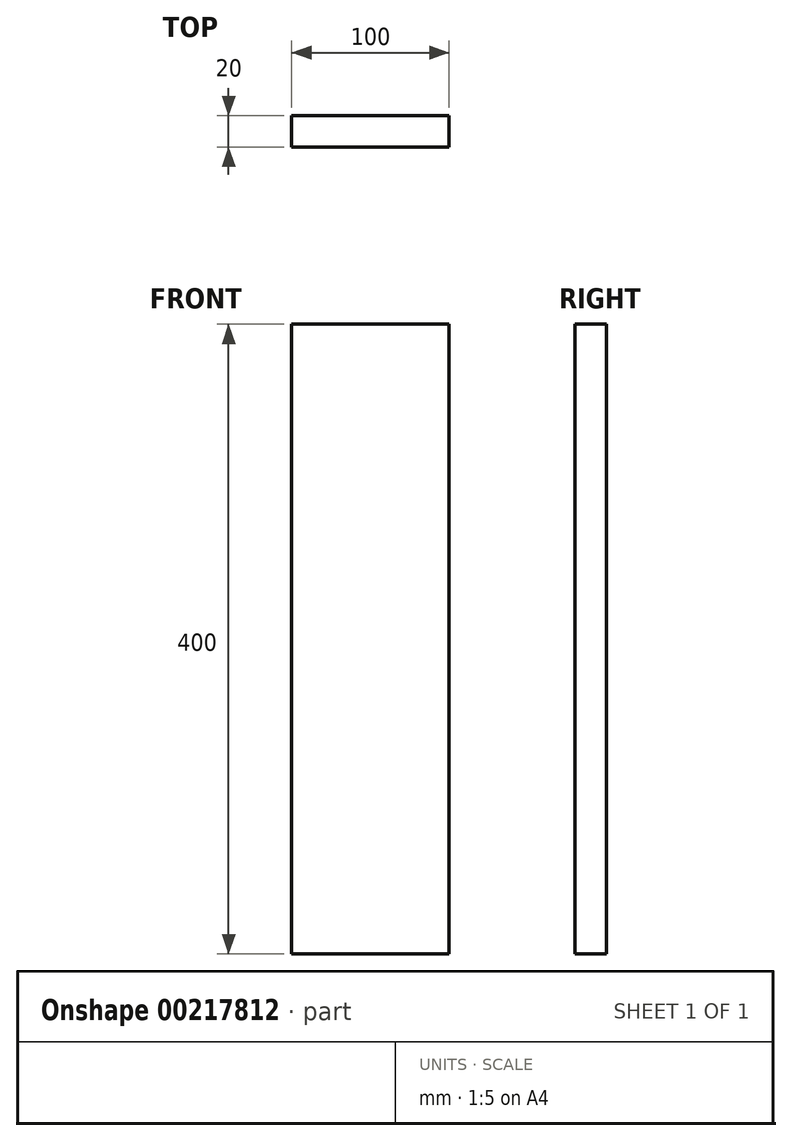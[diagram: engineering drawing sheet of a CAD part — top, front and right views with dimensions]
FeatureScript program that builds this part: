
annotation { "Feature Type Name" : "Feature", "Feature Type Description" : "" }
export const myFeature = defineFeature(function(context is Context, id is Id, definition is map)
    precondition{}
    {
        {
            var Q0;
            Q0=qCreatedBy(makeId("Front.planeOp"),FACE);
            var sketch = newSketch(context, id + "F0", { "sketchPlane" : qUnion([Q0])});
            skLineSegment(sketch, "E0.bottom", {"start": v(0, 0) * mm, "end": v(-40, 0) * mm});
            skLineSegment(sketch, "E0.top", {"start": v(0, 400) * mm, "end": v(-40, 400) * mm});
            skLineSegment(sketch, "E0.left", {"start": v(0, 0) * mm, "end": v(0, 400) * mm});
            skLineSegment(sketch, "E0.right", {"start": v(-40, 0) * mm, "end": v(-40, 400) * mm});
            skPoint(sketch, "E1.firstSnap0", {"position": v(-40, 200) * mm});
            skSolve(sketch);
        }
        {
            var Q0;
            Q0=makeQuery(id+"F0.imprint","IMPRINT",FACE,{"disambiguationData":[TD([[makeQuery(id+"F0.imprint","IMPRINT",EDGE,{"derivedFrom":sQuery(id+"F0.wireOp",EDGE,"E0.bottom")}),-1.0]])]});
            extrude(context, id + "F1", {"entities" : qUnion([Q0]), "depth" : 20 * mm});
        }
        {
            var Q0;
            Q0=qCreatedBy(makeId("Front.planeOp"),FACE);
            var sketch = newSketch(context, id + "F2", { "sketchPlane" : qUnion([Q0])});
            skSolve(sketch);
        }
        {
            var Q0;
            Q0 = qSketchRegion(id + "F2", true);
            var Q1;
            Q1=makeQuery(id+"F1.opExtrude","SWEPT_FACE",FACE,{"disambiguationData":[OSD([sQuery(id+"F0.wireOp",EDGE,"E0.right")])]});
            extrude(context, id + "F3", {"entities" : qUnion([Q0, Q1]), "operationType" : NewBodyOperationType.ADD, "depth" : 60 * mm});
        }
    });
